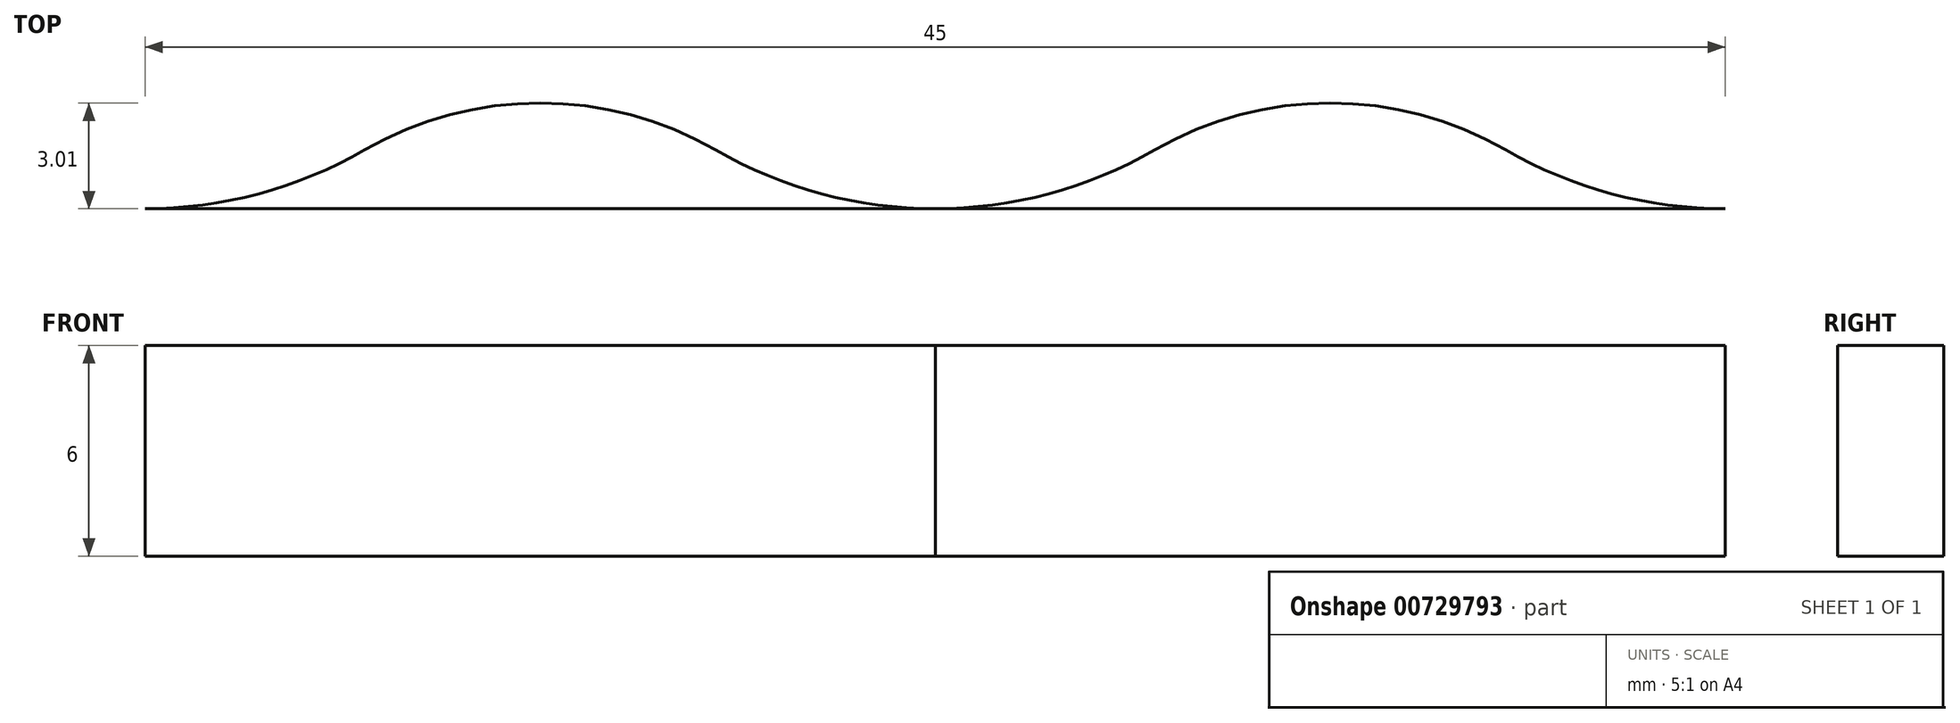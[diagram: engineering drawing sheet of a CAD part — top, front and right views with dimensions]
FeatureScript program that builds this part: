
annotation { "Feature Type Name" : "Feature", "Feature Type Description" : "" }
export const myFeature = defineFeature(function(context is Context, id is Id, definition is map)
    precondition{}
    {
        {
            var Q0;
            Q0=qCreatedBy(makeId("Top.planeOp"),FACE);
            var sketch = newSketch(context, id + "F0", { "sketchPlane" : qUnion([Q0])});
            skLineSegment(sketch, "E0.bottom", {"start": v(-22.5, 12.5) * mm, "end": v(22.5, 12.5) * mm});
            skLineSegment(sketch, "E0.top", {"start": v(-22.5, -12.5) * mm, "end": v(22.5, -12.5) * mm});
            skLineSegment(sketch, "E0.left", {"start": v(-35, 0) * mm, "end": v(-35, 0) * mm});
            skLineSegment(sketch, "E0.right", {"start": v(35, 0) * mm, "end": v(35, 0) * mm});
            skPoint(sketch, "E0.middle", {"position": v(0, 0) * mm});
            skCircle(sketch, "E1", {"center": v(0, 0) * mm, "radius": 9.5 * mm});
            skCircle(sketch, "E2", {"center": v(-22.5, 0) * mm, "radius": 9 * mm});
            skCircle(sketch, "E3", {"center": v(22.5, 0) * mm, "radius": 9 * mm});
            skPoint(sketch, "E4.visualSharp", {"position": v(-35, 12.5) * mm});
            skArc(sketch, "E4.filletArc", {"start": v(-22.5, 12.5) * mm, "mid": v(-31.34, 8.84) * mm, "end": v(-35, 0) * mm});
            skPoint(sketch, "E5.visualSharp", {"position": v(35, 12.5) * mm});
            skArc(sketch, "E5.filletArc", {"start": v(35, 0) * mm, "mid": v(31.34, 8.84) * mm, "end": v(22.5, 12.5) * mm});
            skPoint(sketch, "E6.visualSharp", {"position": v(35, -12.5) * mm});
            skArc(sketch, "E6.filletArc", {"start": v(22.5, -12.5) * mm, "mid": v(31.34, -8.84) * mm, "end": v(35, 0) * mm});
            skPoint(sketch, "E7.visualSharp", {"position": v(-35, -12.5) * mm});
            skArc(sketch, "E7.filletArc", {"start": v(-35, 0) * mm, "mid": v(-31.34, -8.84) * mm, "end": v(-22.5, -12.5) * mm});
            skSolve(sketch);
        }
        {
            var Q0;
            Q0 = qSketchRegion(id + "F0", true);
            extrude(context, id + "F1", {"entities" : qUnion([Q0]), "endBound" : BoundingType.SYMMETRIC, "depth" : 6 * mm, "offsetDistance" : 25 * mm});
        }
        {
            var Q0;
            Q0=makeQuery(id+"F1.opExtrude","CAP_FACE",FACE,{"disambiguationData":[OSD([sQuery(id+"F0.wireOp",EDGE,"E0.bottom"),sQuery(id+"F0.wireOp",EDGE,"E0.top"),sQuery(id+"F0.wireOp",EDGE,"E1"),sQuery(id+"F0.wireOp",EDGE,"E2"),sQuery(id+"F0.wireOp",EDGE,"E3"),sQuery(id+"F0.wireOp",EDGE,"E4.filletArc"),sQuery(id+"F0.wireOp",EDGE,"E5.filletArc"),sQuery(id+"F0.wireOp",EDGE,"E6.filletArc"),sQuery(id+"F0.wireOp",EDGE,"E7.filletArc")])],"isStart":false});
            var sketch = newSketch(context, id + "F2", { "sketchPlane" : qUnion([Q0])});
            skArc(sketch, "E8", {"start": v(-16.25, 10.83) * mm, "mid": v(-19.26, 12.07) * mm, "end": v(-22.5, 12.5) * mm});
            skArc(sketch, "E9", {"start": v(-16.25, 10.83) * mm, "mid": v(-11.25, 9.49) * mm, "end": v(-6.25, 10.83) * mm});
            skArc(sketch, "E10", {"start": v(0, 12.5) * mm, "mid": v(-3.24, 12.07) * mm, "end": v(-6.25, 10.83) * mm});
            skLineSegment(sketch, "E11", {"start": v(-22.5, 12.5) * mm, "end": v(0, 12.5) * mm});
            skLineSegment(sketch, "E12.1.0.0", {"start": v(0, 12.5) * mm, "end": v(22.5, 12.5) * mm});
            skArc(sketch, "E12.1.0.1", {"start": v(22.5, 12.5) * mm, "mid": v(19.26, 12.07) * mm, "end": v(16.25, 10.83) * mm});
            skArc(sketch, "E12.1.0.2", {"start": v(6.25, 10.83) * mm, "mid": v(11.25, 9.49) * mm, "end": v(16.25, 10.83) * mm});
            skArc(sketch, "E12.1.0.3", {"start": v(6.25, 10.83) * mm, "mid": v(3.24, 12.07) * mm, "end": v(0, 12.5) * mm});
            skLineSegment(sketch, "E12.direction1", {"start": v(-16.25, 10.83) * mm, "end": v(6.25, 10.83) * mm, "construction": true});
            skArc(sketch, "E13.MirrorCS", {"start": v(-16.25, -10.83) * mm, "mid": v(-19.26, -12.07) * mm, "end": v(-22.5, -12.5) * mm});
            skArc(sketch, "E14.MirrorCS", {"start": v(-16.25, -10.83) * mm, "mid": v(-11.25, -9.49) * mm, "end": v(-6.25, -10.83) * mm});
            skArc(sketch, "E15.MirrorCS", {"start": v(0, -12.5) * mm, "mid": v(-3.24, -12.07) * mm, "end": v(-6.25, -10.83) * mm});
            skArc(sketch, "E16.MirrorCS", {"start": v(6.25, -10.83) * mm, "mid": v(3.24, -12.07) * mm, "end": v(0, -12.5) * mm});
            skArc(sketch, "E17.MirrorCS", {"start": v(6.25, -10.83) * mm, "mid": v(11.25, -9.49) * mm, "end": v(16.25, -10.83) * mm});
            skArc(sketch, "E18.MirrorCS", {"start": v(22.5, -12.5) * mm, "mid": v(19.26, -12.07) * mm, "end": v(16.25, -10.83) * mm});
            skSolve(sketch);
        }
        {
            var Q0;
            Q0=makeQuery(id+"F2.imprint","IMPRINT",FACE,{"disambiguationData":[TD([[makeQuery(id+"F2.imprint","IMPRINT",EDGE,{"derivedFrom":sQuery(id+"F2.wireOp",EDGE,"E12.1.0.0")}),-1.0]])]});
            var Q1;
            Q1=makeQuery(id+"F2.imprint","IMPRINT",FACE,{"disambiguationData":[TD([[makeQuery(id+"F2.imprint","IMPRINT",EDGE,{"derivedFrom":sQuery(id+"F2.wireOp",EDGE,"E8")}),-1.0]])]});
            var Q2;
            {var subQ0=sQuery(id+"F2.wireOp",EDGE,"E16.MirrorCS");Q2=makeQuery(id+"F2.imprint","IMPRINT",FACE,{"disambiguationData":[TD([[makeQuery(id+"F2.imprint","IMPRINT",EDGE,{"derivedFrom":subQ0}),1.0]])]});}
            var Q3;
            {var subQ0=sQuery(id+"F2.wireOp",EDGE,"E13.MirrorCS");Q3=makeQuery(id+"F2.imprint","IMPRINT",FACE,{"disambiguationData":[TD([[makeQuery(id+"F2.imprint","IMPRINT",EDGE,{"derivedFrom":subQ0}),1.0]])]});}
            extrude(context, id + "F3", {"entities" : qUnion([Q0, Q1, Q2, Q3]), "operationType" : NewBodyOperationType.REMOVE, "endBound" : BoundingType.THROUGH_ALL, "oppositeDirection" : true, "depth" : 25 * mm, "offsetDistance" : 25 * mm});
        }
    });
